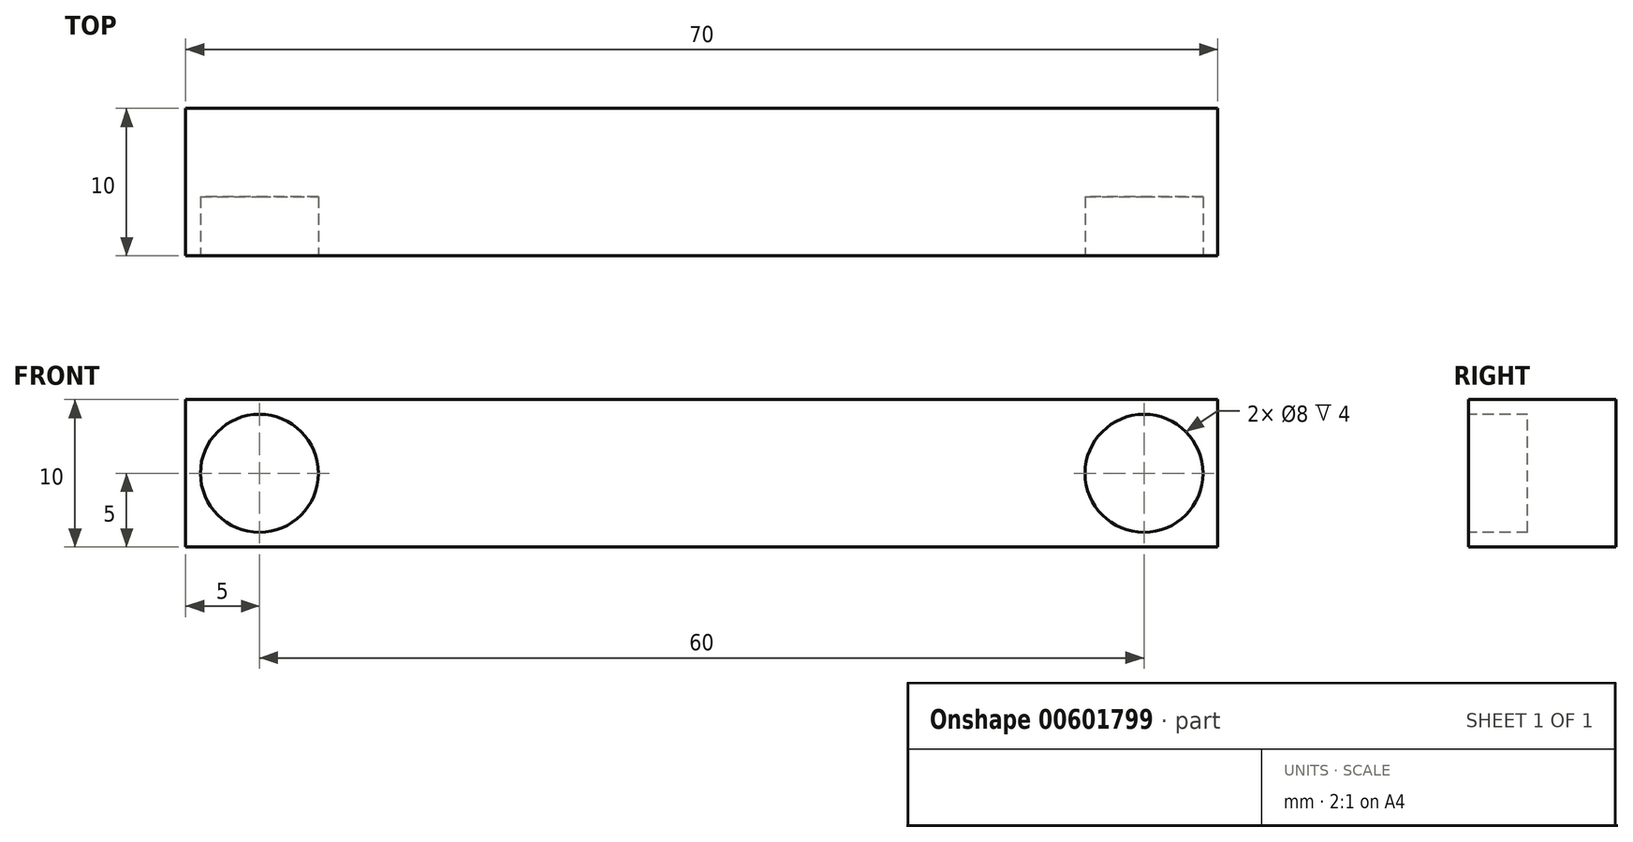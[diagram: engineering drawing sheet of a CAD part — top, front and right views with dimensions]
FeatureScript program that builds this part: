
annotation { "Feature Type Name" : "Feature", "Feature Type Description" : "" }
export const myFeature = defineFeature(function(context is Context, id is Id, definition is map)
    precondition{}
    {
        {
            var Q0;
            Q0=qCreatedBy(makeId("Top.planeOp"),FACE);
            var sketch = newSketch(context, id + "F0", { "sketchPlane" : qUnion([Q0])});
            skLineSegment(sketch, "E0.bottom", {"start": v(-35, 2.5) * mm, "end": v(35, 2.5) * mm});
            skLineSegment(sketch, "E0.top", {"start": v(-35, 12.5) * mm, "end": v(35, 12.5) * mm});
            skLineSegment(sketch, "E0.left", {"start": v(-35, 2.5) * mm, "end": v(-35, 12.5) * mm});
            skLineSegment(sketch, "E0.right", {"start": v(35, 2.5) * mm, "end": v(35, 12.5) * mm});
            skSolve(sketch);
        }
        {
            var Q0;
            Q0=makeQuery(id+"F0.imprint","IMPRINT",FACE,{"disambiguationData":[TD([[makeQuery(id+"F0.imprint","IMPRINT",EDGE,{"derivedFrom":sQuery(id+"F0.wireOp",EDGE,"E0.bottom")}),1.0]])]});
            extrude(context, id + "F1", {"entities" : qUnion([Q0]), "depth" : 10 * mm, "offsetDistance" : 25 * mm});
        }
        {
            var Q0;
            Q0=makeQuery(id+"F1.opExtrude","SWEPT_FACE",FACE,{"disambiguationData":[OSD([sQuery(id+"F0.wireOp",EDGE,"E0.bottom")])]});
            var sketch = newSketch(context, id + "F2", { "sketchPlane" : qUnion([Q0])});
            skCircle(sketch, "E1", {"center": v(30, 5) * mm, "radius": 4 * mm});
            skPoint(sketch, "E1.centerSnap0", {"position": v(35, 5) * mm});
            skCircle(sketch, "E2", {"center": v(-30, 5) * mm, "radius": 4 * mm});
            skPoint(sketch, "E2.centerSnap0", {"position": v(-35, 5) * mm});
            skSolve(sketch);
        }
        {
            var Q0;
            {var subQ0=sQuery(id+"F2.wireOp",EDGE,"E2");var subQ1=sQuery(id+"F0.wireOp",EDGE,"E0.bottom");var subQ2=makeQuery(id+"F2.imprint","INTERSECT",VERTEX,{"derivedFrom":[makeQuery(id+"F1.opExtrude","CAP_EDGE",EDGE,{"disambiguationData":[OSD([subQ1])],"isStart":true}),subQ0]});Q0=makeQuery(id+"F2.imprint","IMPRINT",FACE,{"disambiguationData":[TD([[makeQuery(id+"F2.imprint","IMPRINT",EDGE,{"disambiguationData":[TD([[subQ2,1.0]])],"derivedFrom":subQ0}),1.0]])]});}
            var Q1;
            {var subQ0=sQuery(id+"F2.wireOp",EDGE,"E1");var subQ1=sQuery(id+"F0.wireOp",EDGE,"E0.bottom");var subQ2=makeQuery(id+"F2.imprint","INTERSECT",VERTEX,{"derivedFrom":[makeQuery(id+"F1.opExtrude","CAP_EDGE",EDGE,{"disambiguationData":[OSD([subQ1])],"isStart":true}),subQ0]});Q1=makeQuery(id+"F2.imprint","IMPRINT",FACE,{"disambiguationData":[TD([[makeQuery(id+"F2.imprint","IMPRINT",EDGE,{"disambiguationData":[TD([[subQ2,1.0]])],"derivedFrom":subQ0}),1.0]])]});}
            extrude(context, id + "F3", {"entities" : qUnion([Q0, Q1]), "operationType" : NewBodyOperationType.REMOVE, "oppositeDirection" : true, "depth" : 4 * mm, "offsetDistance" : 25 * mm});
        }
    });
